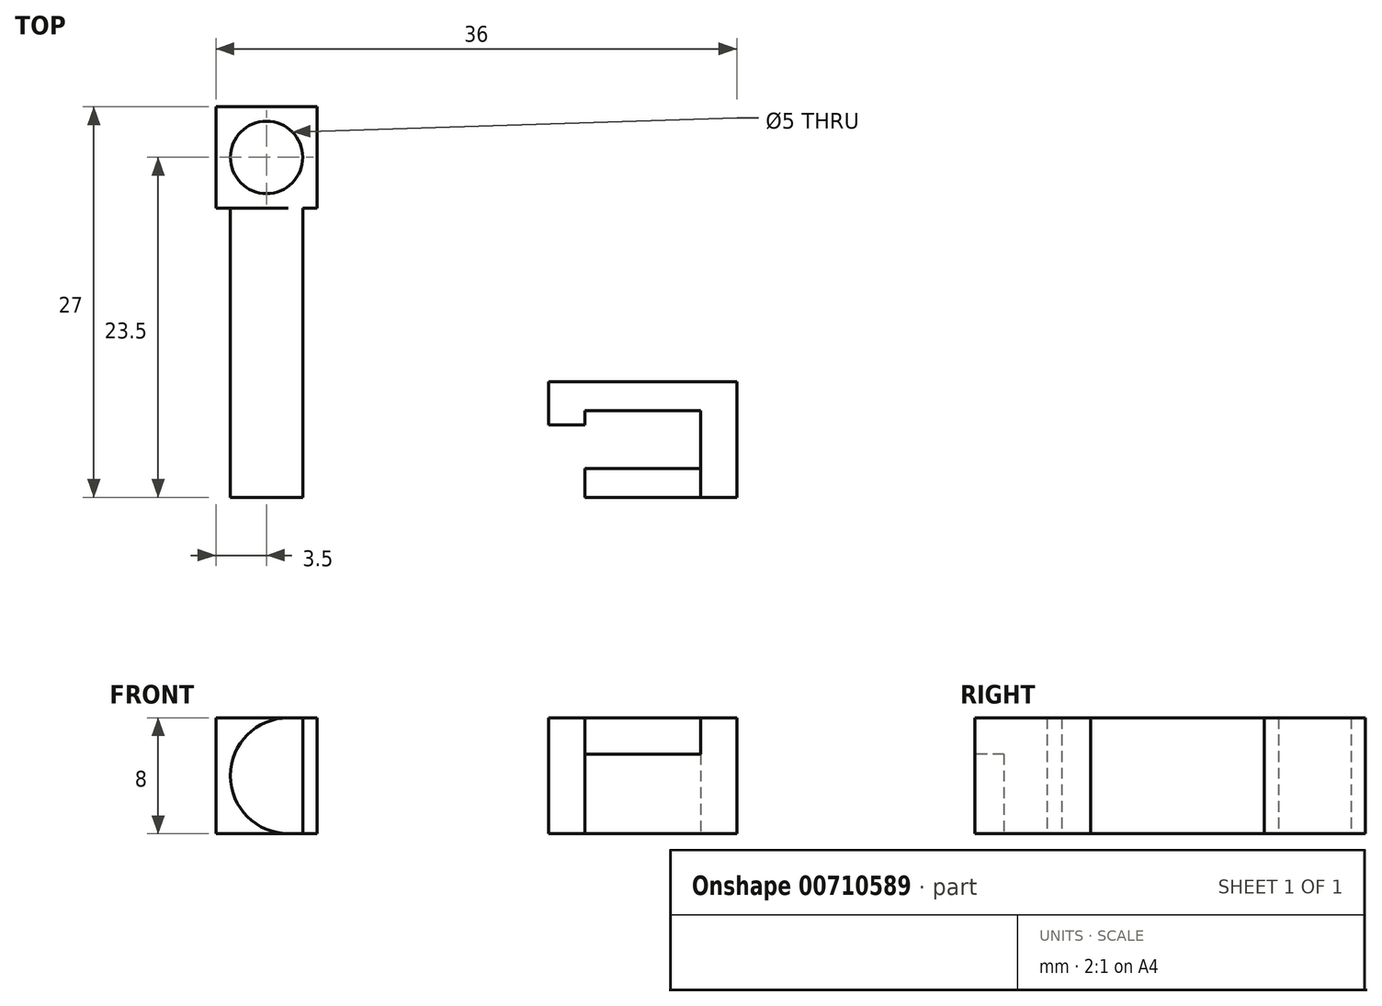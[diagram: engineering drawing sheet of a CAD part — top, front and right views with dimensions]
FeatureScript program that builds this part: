
annotation { "Feature Type Name" : "Feature", "Feature Type Description" : "" }
export const myFeature = defineFeature(function(context is Context, id is Id, definition is map)
    precondition{}
    {
        {
            var Q0;
            Q0=qCreatedBy(makeId("Top.planeOp"),FACE);
            var sketch = newSketch(context, id + "F0", { "sketchPlane" : qUnion([Q0])});
            skLineSegment(sketch, "E0.bottom", {"start": v(2.5, -10) * mm, "end": v(-2.5, -10) * mm});
            skLineSegment(sketch, "E0.top", {"start": v(2.5, 10) * mm, "end": v(-2.5, 10) * mm});
            skLineSegment(sketch, "E0.left", {"start": v(2.5, -10) * mm, "end": v(2.5, 10) * mm});
            skLineSegment(sketch, "E0.right", {"start": v(-2.5, -10) * mm, "end": v(-2.5, 10) * mm});
            skPoint(sketch, "E0.middle", {"position": v(0, 0) * mm});
            skLineSegment(sketch, "E1", {"start": v(-2.5, 10) * mm, "end": v(-3.5, 10) * mm});
            skLineSegment(sketch, "E2", {"start": v(-3.5, 10) * mm, "end": v(-3.5, 17) * mm});
            skLineSegment(sketch, "E3", {"start": v(-3.5, 17) * mm, "end": v(3.5, 17) * mm});
            skLineSegment(sketch, "E4", {"start": v(3.5, 17) * mm, "end": v(3.5, 10) * mm});
            skLineSegment(sketch, "E5", {"start": v(3.5, 10) * mm, "end": v(2.5, 10) * mm});
            skPoint(sketch, "E6.endSnap0", {"position": v(-3.5, 13.5) * mm});
            skPoint(sketch, "E7", {"position": v(0, 13.5) * mm});
            skPoint(sketch, "E7.positionSnap0", {"position": v(0, 10) * mm});
            skCircle(sketch, "E8", {"center": v(0, 13.5) * mm, "radius": 2.5 * mm});
            skLineSegment(sketch, "E9.bottom", {"start": v(2.5, -10) * mm, "end": v(32.5, -10) * mm});
            skLineSegment(sketch, "E9.top", {"start": v(2.5, -5) * mm, "end": v(32.5, -5) * mm});
            skLineSegment(sketch, "E9.left", {"start": v(2.5, -10) * mm, "end": v(2.5, -5) * mm});
            skLineSegment(sketch, "E9.right", {"start": v(32.5, -10) * mm, "end": v(32.5, -5) * mm});
            skLineSegment(sketch, "E10", {"start": v(32.5, -10) * mm, "end": v(30, -10) * mm});
            skLineSegment(sketch, "E11", {"start": v(30, -10) * mm, "end": v(30, -4) * mm});
            skLineSegment(sketch, "E12", {"start": v(30, -4) * mm, "end": v(22, -4) * mm});
            skLineSegment(sketch, "E13", {"start": v(22, -4) * mm, "end": v(22, -10) * mm});
            skLineSegment(sketch, "E14", {"start": v(30, -10) * mm, "end": v(30, -8) * mm});
            skLineSegment(sketch, "E15", {"start": v(30, -8) * mm, "end": v(22, -8) * mm});
            skLineSegment(sketch, "E16", {"start": v(22, -4) * mm, "end": v(19.5, -4) * mm, "construction": true});
            skLineSegment(sketch, "E17", {"start": v(19.5, -4) * mm, "end": v(19.5, -5) * mm});
            skLineSegment(sketch, "E18", {"start": v(19.5, -4) * mm, "end": v(19.5, -2) * mm});
            skLineSegment(sketch, "E19", {"start": v(19.5, -2) * mm, "end": v(32.5, -2) * mm});
            skLineSegment(sketch, "E20", {"start": v(32.5, -2) * mm, "end": v(32.5, -5) * mm});
            skSolve(sketch);
        }
        {
            var Q0;
            Q0=makeQuery(id+"F0.imprint","IMPRINT",FACE,{"disambiguationData":[TD([[makeQuery(id+"F0.imprint","IMPRINT",EDGE,{"derivedFrom":sQuery(id+"F0.wireOp",EDGE,"E0.top")}),-1.0]])]});
            var Q1;
            Q1=makeQuery(id+"F0.imprint","IMPRINT",FACE,{"disambiguationData":[TD([[makeQuery(id+"F0.imprint","IMPRINT",EDGE,{"derivedFrom":sQuery(id+"F0.wireOp",EDGE,"E0.bottom")}),-1.0]])]});
            var Q2;
            Q2=makeQuery(id+"F0.imprint","IMPRINT",FACE,{"disambiguationData":[TD([[makeQuery(id+"F0.imprint","IMPRINT",EDGE,{"derivedFrom":sQuery(id+"F0.wireOp",EDGE,"E9.bottom")}),1.0]])]});
            var Q3;
            {var subQ4=sQuery(id+"F0.wireOp",EDGE,"E9.left");Q3=makeQuery(id+"F0.imprint","IMPRINT",FACE,{"disambiguationData":[TD([[makeQuery(id+"F0.imprint","IMPRINT",EDGE,{"derivedFrom":subQ4}),-1.0]])]});}
            var Q4;
            {var subQ4=sQuery(id+"F0.wireOp",EDGE,"E9.right");Q4=makeQuery(id+"F0.imprint","IMPRINT",FACE,{"disambiguationData":[TD([[makeQuery(id+"F0.imprint","IMPRINT",EDGE,{"derivedFrom":subQ4}),1.0]])]});}
            var Q5;
            {var subQ0=sQuery(id+"F0.wireOp",EDGE,"E12");Q5=makeQuery(id+"F0.imprint","IMPRINT",FACE,{"disambiguationData":[TD([[makeQuery(id+"F0.imprint","IMPRINT",EDGE,{"derivedFrom":subQ0}),-1.0]])]});}
            extrude(context, id + "F1", {"entities" : qUnion([Q0, Q1, Q2, Q3, Q4, Q5]), "depth" : 8 * mm, "offsetDistance" : 25 * mm});
        }
        {
            var Q0;
            Q0=makeQuery(id+"F1.opExtrude","SWEPT_FACE",FACE,{"disambiguationData":[OSD([sQuery(id+"F0.wireOp",EDGE,"E0.bottom"),sQuery(id+"F0.wireOp",EDGE,"E9.bottom"),sQuery(id+"F0.wireOp",EDGE,"E10")])]});
            var sketch = newSketch(context, id + "F2", { "sketchPlane" : qUnion([Q0])});
            skLineSegment(sketch, "E21", {"start": v(32.5, 8) * mm, "end": v(30, 8) * mm});
            skLineSegment(sketch, "E22", {"start": v(30, 8) * mm, "end": v(22, 8) * mm});
            skLineSegment(sketch, "E23", {"start": v(22, 8) * mm, "end": v(22, 5.5) * mm});
            skLineSegment(sketch, "E24", {"start": v(22, 5.5) * mm, "end": v(30, 5.5) * mm});
            skLineSegment(sketch, "E25", {"start": v(30, 5.5) * mm, "end": v(30, 8) * mm});
            skLineSegment(sketch, "E26", {"start": v(30, 5.5) * mm, "end": v(30, 2.5) * mm});
            skLineSegment(sketch, "E27", {"start": v(30, 2.5) * mm, "end": v(22, 2.5) * mm});
            skLineSegment(sketch, "E28", {"start": v(22, 2.5) * mm, "end": v(22, 0) * mm});
            skLineSegment(sketch, "E29", {"start": v(30, 2.5) * mm, "end": v(30, 0) * mm});
            skSolve(sketch);
        }
        {
            var Q0;
            Q0=makeQuery(id+"F2.imprint","IMPRINT",FACE,{"disambiguationData":[TD([[makeQuery(id+"F2.imprint","IMPRINT",EDGE,{"derivedFrom":sQuery(id+"F2.wireOp",EDGE,"E22")}),1.0]])]});
            var Q1;
            Q1=makeQuery(id+"F2.imprint","IMPRINT",FACE,{"disambiguationData":[TD([[makeQuery(id+"F2.imprint","IMPRINT",EDGE,{"derivedFrom":sQuery(id+"F2.wireOp",EDGE,"E27")}),1.0]])]});
            extrude(context, id + "F3", {"entities" : qUnion([Q0, Q1]), "operationType" : NewBodyOperationType.REMOVE, "oppositeDirection" : true, "depth" : 3 * mm, "offsetDistance" : 25 * mm});
        }
        {
            var Q0;
            Q0=makeQuery(id+"F1.opExtrude","CAP_EDGE",EDGE,{"disambiguationData":[OSD([sQuery(id+"F0.wireOp",EDGE,"E0.right")])],"isStart":false});
            var Q1;
            Q1=makeQuery(id+"F1.opExtrude","CAP_EDGE",EDGE,{"disambiguationData":[OSD([sQuery(id+"F0.wireOp",EDGE,"E0.right")])],"isStart":true});
            fillet(context, id + "F4", {"entities" : qUnion([Q0, Q1]), "radius" : 4 * mm, "tangentPropagation" : true, "allowEdgeOverflow" : false});
        }
    });
